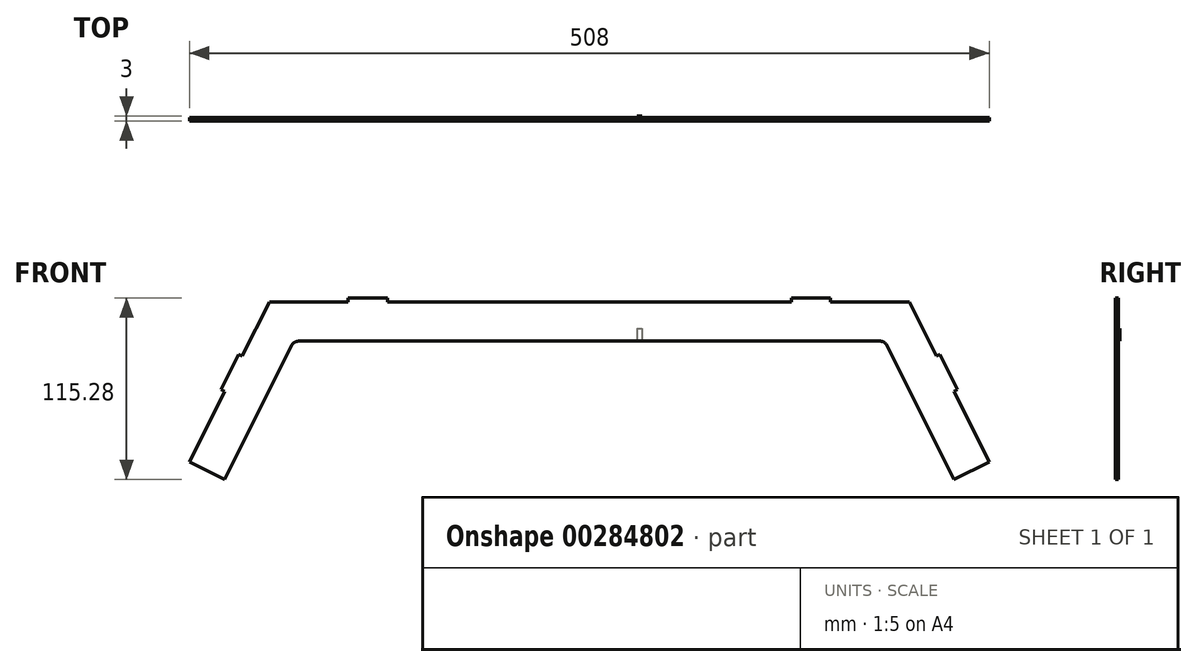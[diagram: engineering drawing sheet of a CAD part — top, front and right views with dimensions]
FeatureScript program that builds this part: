
annotation { "Feature Type Name" : "Feature", "Feature Type Description" : "" }
export const myFeature = defineFeature(function(context is Context, id is Id, definition is map)
    precondition{}
    {
        {
            var Q0;
            Q0=qCreatedBy(makeId("Front.planeOp"),FACE);
            var sketch = newSketch(context, id + "F0", { "sketchPlane" : qUnion([Q0])});
            skLineSegment(sketch, "E0.bottom", {"start": v(-307.35, -195.99) * mm, "end": v(200.65, -195.99) * mm});
            skLineSegment(sketch, "E0.left", {"start": v(-307.35, -195.99) * mm, "end": v(-307.35, 210.41) * mm});
            skLineSegment(sketch, "E0.right", {"start": v(200.65, -195.99) * mm, "end": v(200.65, 210.41) * mm});
            skLineSegment(sketch, "E1", {"start": v(-307.35, 210.41) * mm, "end": v(-256.55, 312.01) * mm});
            skLineSegment(sketch, "E2", {"start": v(-256.55, 312.01) * mm, "end": v(149.85, 312.01) * mm});
            skLineSegment(sketch, "E3", {"start": v(149.85, 312.01) * mm, "end": v(200.65, 210.41) * mm});
            skSolve(sketch);
        }
        {
            var Q0;
            Q0=qSketchRegion(id+"F0",true);
            extrude(context, id + "F1", {"entities" : qUnion([Q0]), "depth" : 2 * mm});
        }
        {
            var Q0;
            Q0=makeQuery(id+"F1.opExtrude","CAP_FACE",FACE,{"disambiguationData":[OSD([sQuery(id+"F0.wireOp",EDGE,"E0.bottom"),sQuery(id+"F0.wireOp",EDGE,"E0.left"),sQuery(id+"F0.wireOp",EDGE,"E0.right"),sQuery(id+"F0.wireOp",EDGE,"E1"),sQuery(id+"F0.wireOp",EDGE,"E2"),sQuery(id+"F0.wireOp",EDGE,"E3")])],"isStart":false});
            var sketch = newSketch(context, id + "F2", { "sketchPlane" : qUnion([Q0])});
            skLineSegment(sketch, "E4.bottom", {"start": v(-205.75, 210.41) * mm, "end": v(99.05, 210.41) * mm});
            skLineSegment(sketch, "E4.top", {"start": v(-205.75, -145.19) * mm, "end": v(99.05, -145.19) * mm});
            skLineSegment(sketch, "E4.left", {"start": v(-256.55, 159.61) * mm, "end": v(-256.55, -94.39) * mm});
            skLineSegment(sketch, "E4.right", {"start": v(149.85, 159.61) * mm, "end": v(149.85, -94.39) * mm});
            skPoint(sketch, "E5.visualSharp", {"position": v(-256.55, 210.41) * mm});
            skArc(sketch, "E5.filletArc", {"start": v(-205.75, 210.41) * mm, "mid": v(-241.67, 195.53) * mm, "end": v(-256.55, 159.61) * mm});
            skPoint(sketch, "E6.visualSharp", {"position": v(149.85, 210.41) * mm});
            skArc(sketch, "E6.filletArc", {"start": v(149.85, 159.61) * mm, "mid": v(134.97, 195.53) * mm, "end": v(99.05, 210.41) * mm});
            skPoint(sketch, "E7.visualSharp", {"position": v(149.85, -145.19) * mm});
            skArc(sketch, "E7.filletArc", {"start": v(99.05, -145.19) * mm, "mid": v(134.97, -130.3) * mm, "end": v(149.85, -94.39) * mm});
            skPoint(sketch, "E8.visualSharp", {"position": v(-256.55, -145.19) * mm});
            skArc(sketch, "E8.filletArc", {"start": v(-256.55, -94.39) * mm, "mid": v(-241.67, -130.3) * mm, "end": v(-205.75, -145.19) * mm});
            skSolve(sketch);
        }
        {
            var Q0;
            Q0=qSketchRegion(id+"F2",true);
            extrude(context, id + "F3", {"entities" : qUnion([Q0]), "operationType" : NewBodyOperationType.REMOVE, "endBound" : BoundingType.THROUGH_ALL, "oppositeDirection" : true, "depth" : 25 * mm});
        }
        {
            var Q0;
            {var subQ0=sQuery(id+"F0.wireOp",EDGE,"E3");var subQ1=sQuery(id+"F0.wireOp",EDGE,"E0.bottom");var subQ2=sQuery(id+"F0.wireOp",EDGE,"E2");var subQ3=sQuery(id+"F0.wireOp",EDGE,"E1");var subQ4=sQuery(id+"F0.wireOp",EDGE,"E0.left");var subQ5=sQuery(id+"F0.wireOp",EDGE,"E0.right");Q0=makeQuery(id+"F3.boolean.opBoolean","SPLIT",FACE,{"disambiguationData":[TD([makeQuery(id+"F1.opExtrude","SWEPT_FACE",FACE,{"disambiguationData":[OSD([subQ1])]})])],"derivedFrom":makeQuery(id+"F1.opExtrude","CAP_FACE",FACE,{"disambiguationData":[OSD([subQ1,subQ4,subQ5,subQ3,subQ2,subQ0])],"isStart":false})});}
            var sketch = newSketch(context, id + "F4", { "sketchPlane" : qUnion([Q0])});
            skLineSegment(sketch, "E9.bottom", {"start": v(-22.97, 295.25) * mm, "end": v(-19.97, 295.25) * mm});
            skLineSegment(sketch, "E9.top", {"start": v(-22.97, 225.47) * mm, "end": v(-19.97, 225.47) * mm});
            skLineSegment(sketch, "E9.left", {"start": v(-22.97, 295.25) * mm, "end": v(-22.97, 225.47) * mm});
            skLineSegment(sketch, "E9.right", {"start": v(-19.97, 295.25) * mm, "end": v(-19.97, 225.47) * mm});
            skSolve(sketch);
        }
        {
            var Q0;
            Q0=qSketchRegion(id+"F4",true);
            extrude(context, id + "F5", {"entities" : qUnion([Q0]), "operationType" : NewBodyOperationType.ADD, "oppositeDirection" : true, "depth" : 3 * mm});
        }
        {
            var Q0;
            {var subQ0=sQuery(id+"F0.wireOp",EDGE,"E3");var subQ1=sQuery(id+"F0.wireOp",EDGE,"E2");var subQ2=sQuery(id+"F0.wireOp",EDGE,"E1");var subQ3=sQuery(id+"F0.wireOp",EDGE,"E0.right");var subQ4=sQuery(id+"F0.wireOp",EDGE,"E0.left");var subQ5=sQuery(id+"F0.wireOp",EDGE,"E0.bottom");var subQ6=makeQuery(id+"F1.opExtrude","CAP_FACE",FACE,{"disambiguationData":[OSD([subQ5,subQ4,subQ3,subQ2,subQ1,subQ0])],"isStart":false});Q0=makeQuery(id+"F5.boolean.opBoolean","MERGE",FACE,{"derivedFrom":[makeQuery(id+"F3.boolean.opBoolean","SPLIT",FACE,{"disambiguationData":[TD([makeQuery(id+"F1.opExtrude","SWEPT_FACE",FACE,{"disambiguationData":[OSD([subQ5])]})])],"derivedFrom":subQ6}),makeQuery(id+"F3.boolean.opBoolean","SPLIT",FACE,{"disambiguationData":[TD([makeQuery(id+"F3.opExtrude","SWEPT_FACE",FACE,{"disambiguationData":[OSD([sQuery(id+"F2.wireOp",EDGE,"37a97e87-8427-4c95-81a0-ebdeb4e0e8c7.sketch_text.stroke-54")])]})])],"derivedFrom":subQ6}),makeQuery(id+"F5.opExtrude","CAP_FACE",FACE,{"disambiguationData":[OSD([sQuery(id+"F4.wireOp",EDGE,"E9.bottom"),sQuery(id+"F4.wireOp",EDGE,"E9.top"),sQuery(id+"F4.wireOp",EDGE,"E9.left"),sQuery(id+"F4.wireOp",EDGE,"E9.right")])],"isStart":true})]});}
            var sketch = newSketch(context, id + "F6", { "sketchPlane" : qUnion([Q0])});
            skPoint(sketch, "E10", {"position": v(-294.85, 185.01) * mm});
            skPoint(sketch, "E11", {"position": v(-294.85, 7.21) * mm});
            skPoint(sketch, "E12", {"position": v(-294.85, -170.59) * mm});
            skPoint(sketch, "E13", {"position": v(188.15, 185.01) * mm});
            skPoint(sketch, "E14", {"position": v(188.15, 7.21) * mm});
            skPoint(sketch, "E15", {"position": v(188.15, -170.59) * mm});
            skSolve(sketch);
        }
        {
            var Q0;
            Q0=sQuery(id+"F6.wireOp",VERTEX,"E10");
            var Q1;
            Q1=sQuery(id+"F6.wireOp",VERTEX,"E11");
            var Q2;
            Q2=sQuery(id+"F6.wireOp",VERTEX,"E12");
            var Q3;
            Q3=sQuery(id+"F6.wireOp",VERTEX,"E15");
            var Q4;
            Q4=sQuery(id+"F6.wireOp",VERTEX,"E14");
            var Q5;
            Q5=sQuery(id+"F6.wireOp",VERTEX,"E13");
            var Q6;
            Q6=makeQuery(id+"F3.boolean.opBoolean","SPLIT",BODY,{"disambiguationData":[OD(0.0)],"derivedFrom":makeQuery(id+"F1.opExtrude","SWEPT_BODY",BODY,{"disambiguationData":[OSD([sQuery(id+"F0.wireOp",EDGE,"E0.bottom"),sQuery(id+"F0.wireOp",EDGE,"E0.left"),sQuery(id+"F0.wireOp",EDGE,"E0.right"),sQuery(id+"F0.wireOp",EDGE,"E1"),sQuery(id+"F0.wireOp",EDGE,"E2"),sQuery(id+"F0.wireOp",EDGE,"E3")])]})});
            hole(context, id + "F7", {"style" : HoleStyle.SIMPLE, "endStyle" : HoleEndStyle.THROUGH, "standardTappedOrClearance" : lookupTablePath({ "standard" : "ISO", "fit" : "Normal", "size" : "M6", "type" : "Clearance" }), "standardBlindInLast" : lookupTablePath({ "fit" : "Standard", "standard" : "ISO", "size" : "M6", "type" : "Clearance" }), "holeDiameter" : 6.6 * mm, "tappedDepth" : 12 * mm, "tapClearance" : 3, "locations" : qUnion([Q0, Q1, Q2, Q3, Q4, Q5]), "scope" : qUnion([Q6])});
        }
        {
            var Q0;
            Q0=makeQuery(id+"F1.opExtrude","CAP_FACE",FACE,{"disambiguationData":[OSD([sQuery(id+"F0.wireOp",EDGE,"E0.bottom"),sQuery(id+"F0.wireOp",EDGE,"E0.left"),sQuery(id+"F0.wireOp",EDGE,"E0.right"),sQuery(id+"F0.wireOp",EDGE,"E1"),sQuery(id+"F0.wireOp",EDGE,"E2"),sQuery(id+"F0.wireOp",EDGE,"E3")])],"isStart":false});
            var sketch = newSketch(context, id + "F8", { "sketchPlane" : qUnion([Q0])});
            skLineSegment(sketch, "E16", {"start": v(-307.35, 210.41) * mm, "end": v(-284.99, 199.23) * mm});
            skLineSegment(sketch, "E17", {"start": v(-284.99, 199.23) * mm, "end": v(-242.48, 284.25) * mm});
            skLineSegment(sketch, "E18", {"start": v(-238, 287.01) * mm, "end": v(131.31, 287.01) * mm});
            skLineSegment(sketch, "E19", {"start": v(135.78, 284.25) * mm, "end": v(178.3, 199.23) * mm});
            skLineSegment(sketch, "E20", {"start": v(178.3, 199.23) * mm, "end": v(200.65, 210.41) * mm});
            skLineSegment(sketch, "E21", {"start": v(200.65, 210.41) * mm, "end": v(200.65, -195.99) * mm});
            skLineSegment(sketch, "E22", {"start": v(200.65, -195.99) * mm, "end": v(-307.35, -195.99) * mm});
            skLineSegment(sketch, "E23", {"start": v(-307.35, -195.99) * mm, "end": v(-307.35, 210.41) * mm});
            skPoint(sketch, "E24.visualSharp", {"position": v(-241.1, 287.01) * mm});
            skArc(sketch, "E24.filletArc", {"start": v(-238, 287.01) * mm, "mid": v(-240.63, 286.26) * mm, "end": v(-242.48, 284.25) * mm});
            skPoint(sketch, "E25.visualSharp", {"position": v(134.4, 287.01) * mm});
            skArc(sketch, "E25.filletArc", {"start": v(135.78, 284.25) * mm, "mid": v(133.94, 286.26) * mm, "end": v(131.31, 287.01) * mm});
            skSolve(sketch);
        }
        {
            var Q0;
            Q0 = qSketchRegion(id + "F8", true);
            extrude(context, id + "F9", {"entities" : qUnion([Q0]), "operationType" : NewBodyOperationType.REMOVE, "oppositeDirection" : true, "depth" : 25 * mm, "offsetDistance" : 25 * mm});
        }
        {
            var Q0;
            Q0=makeQuery(id+"F1.opExtrude","CAP_FACE",FACE,{"disambiguationData":[OSD([sQuery(id+"F0.wireOp",EDGE,"E0.bottom"),sQuery(id+"F0.wireOp",EDGE,"E0.left"),sQuery(id+"F0.wireOp",EDGE,"E0.right"),sQuery(id+"F0.wireOp",EDGE,"E1"),sQuery(id+"F0.wireOp",EDGE,"E2"),sQuery(id+"F0.wireOp",EDGE,"E3")])],"isStart":false});
            var sketch = newSketch(context, id + "F10", { "sketchPlane" : qUnion([Q0])});
            skLineSegment(sketch, "E26.bottom", {"start": v(-206.55, 312.01) * mm, "end": v(-181.55, 312.01) * mm});
            skLineSegment(sketch, "E26.top", {"start": v(-206.55, 314.51) * mm, "end": v(-181.55, 314.51) * mm});
            skLineSegment(sketch, "E26.left", {"start": v(-206.55, 312.01) * mm, "end": v(-206.55, 314.51) * mm});
            skLineSegment(sketch, "E26.right", {"start": v(-181.55, 312.01) * mm, "end": v(-181.55, 314.51) * mm});
            skLineSegment(sketch, "E27.bottom", {"start": v(74.85, 312.01) * mm, "end": v(99.85, 312.01) * mm});
            skLineSegment(sketch, "E27.top", {"start": v(74.85, 314.51) * mm, "end": v(99.85, 314.51) * mm});
            skLineSegment(sketch, "E27.left", {"start": v(74.85, 312.01) * mm, "end": v(74.85, 314.51) * mm});
            skLineSegment(sketch, "E27.right", {"start": v(99.85, 312.01) * mm, "end": v(99.85, 314.51) * mm});
            skLineSegment(sketch, "E28", {"start": v(-273.8, 277.5) * mm, "end": v(-276.04, 278.61) * mm});
            skLineSegment(sketch, "E29", {"start": v(-276.04, 278.61) * mm, "end": v(-287.22, 256.25) * mm});
            skLineSegment(sketch, "E30", {"start": v(-287.22, 256.25) * mm, "end": v(-284.99, 255.13) * mm});
            skLineSegment(sketch, "E31", {"start": v(-284.99, 255.13) * mm, "end": v(-273.8, 277.5) * mm});
            skLineSegment(sketch, "E32", {"start": v(167.11, 277.5) * mm, "end": v(178.3, 255.13) * mm});
            skLineSegment(sketch, "E33", {"start": v(178.3, 255.13) * mm, "end": v(180.53, 256.25) * mm});
            skLineSegment(sketch, "E34", {"start": v(180.53, 256.25) * mm, "end": v(169.35, 278.61) * mm});
            skLineSegment(sketch, "E35", {"start": v(169.35, 278.61) * mm, "end": v(167.11, 277.5) * mm});
            skSolve(sketch);
        }
        {
            var Q0;
            Q0 = qSketchRegion(id + "F10", true);
            extrude(context, id + "F11", {"entities" : qUnion([Q0]), "operationType" : NewBodyOperationType.ADD, "oppositeDirection" : true, "depth" : 2 * mm, "offsetDistance" : 25 * mm});
        }
    });
